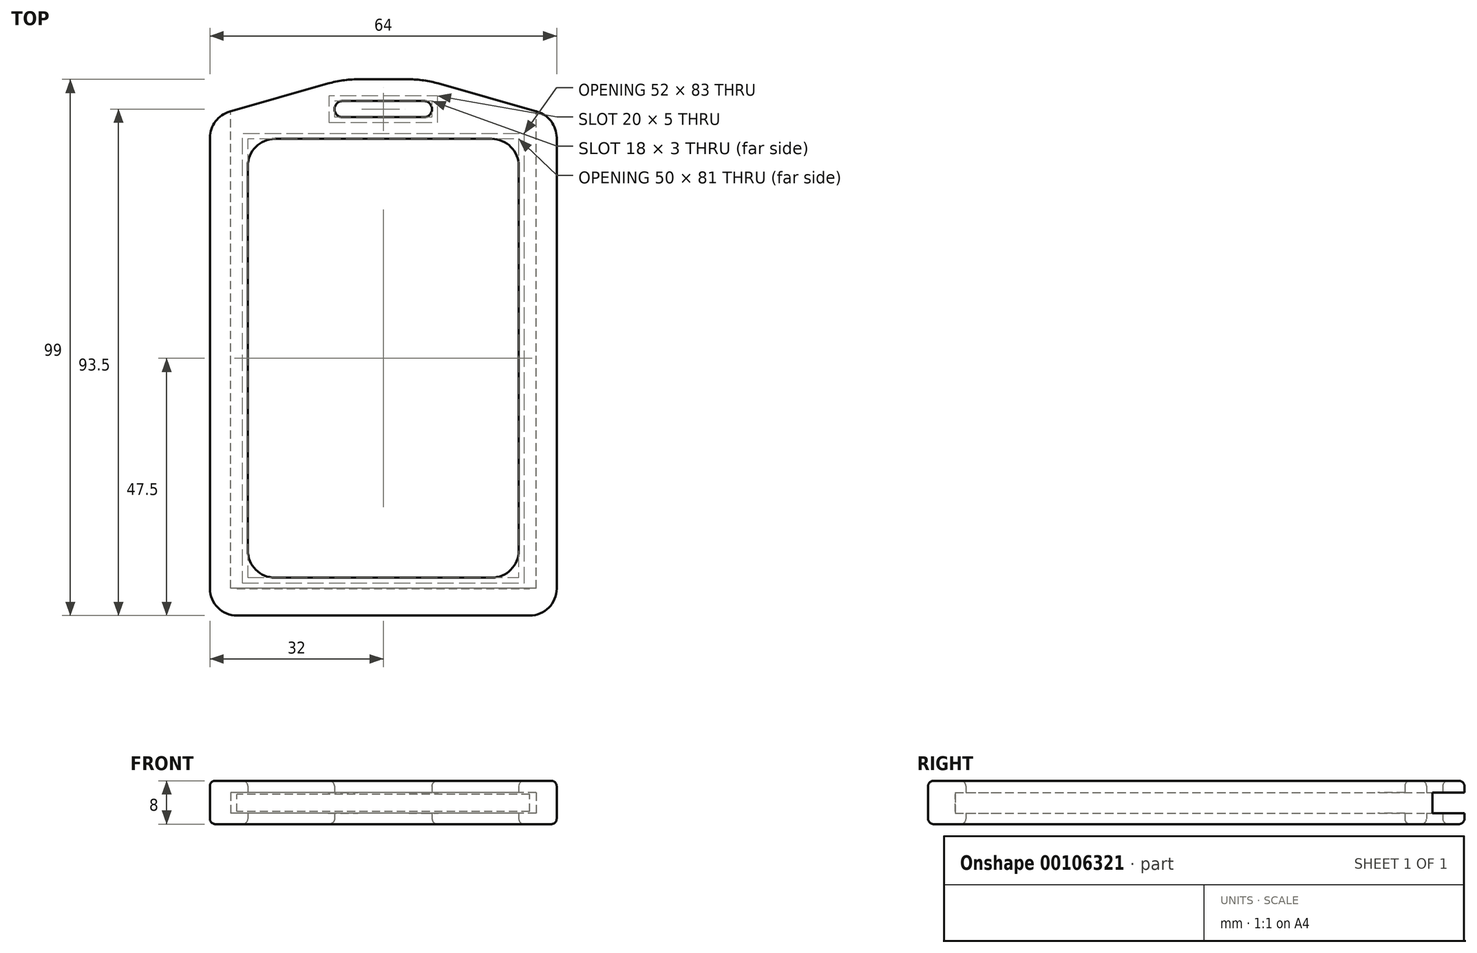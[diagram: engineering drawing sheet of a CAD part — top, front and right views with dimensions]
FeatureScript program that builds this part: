
annotation { "Feature Type Name" : "Feature", "Feature Type Description" : "" }
export const myFeature = defineFeature(function(context is Context, id is Id, definition is map)
    precondition{}
    {
        {
            var Q0;
            Q0=qCreatedBy(makeId("Top.planeOp"),FACE);
            var sketch = newSketch(context, id + "F0", { "sketchPlane" : qUnion([Q0])});
            skLineSegment(sketch, "E0.rect.bottom", {"start": v(-27, 42.5) * mm, "end": v(27, 42.5) * mm});
            skLineSegment(sketch, "E0.rect.top", {"start": v(-27, -42.5) * mm, "end": v(27, -42.5) * mm});
            skLineSegment(sketch, "E0.rect.left", {"start": v(-27, 42.5) * mm, "end": v(-27, -42.5) * mm});
            skLineSegment(sketch, "E0.rect.right", {"start": v(27, 42.5) * mm, "end": v(27, -42.5) * mm});
            skPoint(sketch, "E0.rect.middle", {"position": v(0, 0) * mm});
            skSolve(sketch);
        }
        {
            var Q0;
            Q0=makeQuery(id+"F0.imprint","IMPRINT",FACE,{"disambiguationData":[TD([[makeQuery(id+"F0.imprint","IMPRINT",EDGE,{"derivedFrom":sQuery(id+"F0.wireOp",EDGE,"E0.rect.bottom")}),-1.0]])]});
            extrude(context, id + "F1", {"entities" : qUnion([Q0]), "depth" : 3.2 * mm});
        }
        {
            var Q0;
            Q0=qCreatedBy(makeId("Top.planeOp"),FACE);
            var sketch = newSketch(context, id + "F2", { "sketchPlane" : qUnion([Q0])});
            skLineSegment(sketch, "E1", {"start": v(-32, -47.5) * mm, "end": v(-32, 44.5) * mm});
            skLineSegment(sketch, "E2", {"start": v(32, 44.5) * mm, "end": v(32, -47.5) * mm});
            skLineSegment(sketch, "E3", {"start": v(32, -47.5) * mm, "end": v(-32, -47.5) * mm});
            skLineSegment(sketch, "E4", {"start": v(-7.5, 47.5) * mm, "end": v(7.5, 47.5) * mm});
            skLineSegment(sketch, "E5", {"start": v(-7.5, 44.5) * mm, "end": v(7.5, 44.5) * mm});
            skArc(sketch, "E6", {"start": v(-7.5, 47.5) * mm, "mid": v(-9, 46) * mm, "end": v(-7.5, 44.5) * mm});
            skArc(sketch, "E7", {"start": v(7.5, 47.5) * mm, "mid": v(9, 46) * mm, "end": v(7.5, 44.5) * mm});
            skLineSegment(sketch, "E8.rect.bottom", {"start": v(-25, 40.5) * mm, "end": v(25, 40.5) * mm});
            skLineSegment(sketch, "E8.rect.top", {"start": v(-25, -40.5) * mm, "end": v(25, -40.5) * mm});
            skLineSegment(sketch, "E8.rect.left", {"start": v(-25, 40.5) * mm, "end": v(-25, -40.5) * mm});
            skLineSegment(sketch, "E8.rect.right", {"start": v(25, 40.5) * mm, "end": v(25, -40.5) * mm});
            skPoint(sketch, "E8.rect.middle", {"position": v(0, 0) * mm});
            skLineSegment(sketch, "E9", {"start": v(-32, 44.5) * mm, "end": v(-7.5, 51.5) * mm});
            skLineSegment(sketch, "E10", {"start": v(-7.5, 51.5) * mm, "end": v(7.5, 51.5) * mm});
            skLineSegment(sketch, "E11", {"start": v(7.5, 51.5) * mm, "end": v(32, 44.5) * mm});
            skSolve(sketch);
        }
        {
            var Q0;
            Q0=makeQuery(id+"F2.imprint","IMPRINT",FACE,{"disambiguationData":[TD([[makeQuery(id+"F2.imprint","IMPRINT",EDGE,{"derivedFrom":sQuery(id+"F2.wireOp",EDGE,"E1")}),-1.0]])]});
            var Q1;
            Q1=makeQuery(id+"F2.imprint","IMPRINT",FACE,{"disambiguationData":[TD([[makeQuery(id+"F2.imprint","IMPRINT",EDGE,{"derivedFrom":sQuery(id+"F2.wireOp",EDGE,"E8.rect.bottom")}),1.0]])]});
            extrude(context, id + "F3", {"entities" : qUnion([Q0, Q1]), "depth" : 8 * mm});
        }
        {
            var Q0;
            Q0=makeQuery(id+"F3.opExtrude","SWEPT_EDGE",EDGE,{"disambiguationData":[OSD([sQuery(id+"F2.wireOp",EDGE,"E1"),sQuery(id+"F2.wireOp",EDGE,"bdb59242-d5a5-46b9-b7b7-c48a45b36775")])]});
            var Q1;
            Q1=makeQuery(id+"F3.opExtrude","SWEPT_EDGE",EDGE,{"disambiguationData":[OSD([sQuery(id+"F2.wireOp",EDGE,"daee0165-ca23-428e-b79d-c411e0a02959"),sQuery(id+"F2.wireOp",EDGE,"E2")])]});
            var Q2;
            Q2=makeQuery(id+"F3.opExtrude","SWEPT_EDGE",EDGE,{"disambiguationData":[OSD([sQuery(id+"F2.wireOp",EDGE,"E2"),sQuery(id+"F2.wireOp",EDGE,"E3")])]});
            var Q3;
            Q3=makeQuery(id+"F3.opExtrude","SWEPT_EDGE",EDGE,{"disambiguationData":[OSD([sQuery(id+"F2.wireOp",EDGE,"E1"),sQuery(id+"F2.wireOp",EDGE,"E3")])]});
            fillet(context, id + "F4", {"entities" : qUnion([Q0, Q1, Q2, Q3]), "radius" : 5 * mm, "tangentPropagation" : true, "allowEdgeOverflow" : false});
        }
        {
            var Q0;
            Q0=makeQuery(id+"F3.opExtrude","SWEPT_EDGE",EDGE,{"disambiguationData":[OSD([sQuery(id+"F2.wireOp",EDGE,"E9"),sQuery(id+"F2.wireOp",EDGE,"E10")])]});
            var Q1;
            Q1=makeQuery(id+"F3.opExtrude","SWEPT_EDGE",EDGE,{"disambiguationData":[OSD([sQuery(id+"F2.wireOp",EDGE,"E10"),sQuery(id+"F2.wireOp",EDGE,"E11")])]});
            fillet(context, id + "F5", {"entities" : qUnion([Q0, Q1]), "radius" : 20 * mm, "tangentPropagation" : true, "allowEdgeOverflow" : false});
        }
        {
            var Q0;
            Q0=makeQuery(id+"F3.opExtrude","CAP_EDGE",EDGE,{"disambiguationData":[OSD([sQuery(id+"F2.wireOp",EDGE,"E4")])],"isStart":false});
            var Q1;
            Q1=makeQuery(id+"F3.opExtrude","CAP_EDGE",EDGE,{"disambiguationData":[OSD([sQuery(id+"F2.wireOp",EDGE,"E4")])],"isStart":true});
            fillet(context, id + "F6", {"entities" : qUnion([Q0, Q1]), "radius" : 1 * mm, "tangentPropagation" : true, "allowEdgeOverflow" : false});
        }
        {
            var Q0;
            Q0=makeQuery(id+"F3.opExtrude","SWEPT_EDGE",EDGE,{"disambiguationData":[OSD([sQuery(id+"F2.wireOp",EDGE,"E8.rect.bottom"),sQuery(id+"F2.wireOp",EDGE,"E8.rect.left")])]});
            var Q1;
            Q1=makeQuery(id+"F3.opExtrude","SWEPT_EDGE",EDGE,{"disambiguationData":[OSD([sQuery(id+"F2.wireOp",EDGE,"E8.rect.bottom"),sQuery(id+"F2.wireOp",EDGE,"E8.rect.right")])]});
            var Q2;
            Q2=makeQuery(id+"F3.opExtrude","SWEPT_EDGE",EDGE,{"disambiguationData":[OSD([sQuery(id+"F2.wireOp",EDGE,"E8.rect.top"),sQuery(id+"F2.wireOp",EDGE,"E8.rect.right")])]});
            var Q3;
            Q3=makeQuery(id+"F3.opExtrude","SWEPT_EDGE",EDGE,{"disambiguationData":[OSD([sQuery(id+"F2.wireOp",EDGE,"E8.rect.top"),sQuery(id+"F2.wireOp",EDGE,"E8.rect.left")])]});
            fillet(context, id + "F7", {"entities" : qUnion([Q0, Q1, Q2, Q3]), "radius" : 5 * mm, "tangentPropagation" : true, "allowEdgeOverflow" : false});
        }
        {
            var Q0;
            Q0=makeQuery(id+"F3.opExtrude","CAP_EDGE",EDGE,{"disambiguationData":[OSD([sQuery(id+"F2.wireOp",EDGE,"E8.rect.bottom")])],"isStart":false});
            var Q1;
            Q1=makeQuery(id+"F3.opExtrude","CAP_EDGE",EDGE,{"disambiguationData":[OSD([sQuery(id+"F2.wireOp",EDGE,"E8.rect.bottom")])],"isStart":true});
            var Q2;
            {var subQ0=sQuery(id+"F2.wireOp",EDGE,"E1");var subQ1=sQuery(id+"F2.wireOp",EDGE,"E3");Q2=makeQuery(id+"F4.opFillet","BLEND_EDGE",EDGE,{"blendedFrom":[makeQuery(id+"F3.opExtrude","SWEPT_EDGE",EDGE,{"disambiguationData":[OSD([subQ0,subQ1])]}),makeQuery(id+"F3.opExtrude","CAP_FACE",FACE,{"disambiguationData":[OSD([subQ0,sQuery(id+"F2.wireOp",EDGE,"bdb59242-d5a5-46b9-b7b7-c48a45b36775"),sQuery(id+"F2.wireOp",EDGE,"823fc3bd-2c2f-4f9b-bb1d-b0eb3bebb9c6"),sQuery(id+"F2.wireOp",EDGE,"daee0165-ca23-428e-b79d-c411e0a02959"),sQuery(id+"F2.wireOp",EDGE,"E2"),subQ1,sQuery(id+"F2.wireOp",EDGE,"E4"),sQuery(id+"F2.wireOp",EDGE,"E5"),sQuery(id+"F2.wireOp",EDGE,"E6"),sQuery(id+"F2.wireOp",EDGE,"E7"),sQuery(id+"F2.wireOp",EDGE,"E8.rect.bottom"),sQuery(id+"F2.wireOp",EDGE,"E8.rect.top"),sQuery(id+"F2.wireOp",EDGE,"E8.rect.left"),sQuery(id+"F2.wireOp",EDGE,"E8.rect.right")])],"isStart":false})],"blendedInto":[makeQuery(id+"F3.opExtrude","CAP_FACE",FACE,{"disambiguationData":[OSD([subQ0,sQuery(id+"F2.wireOp",EDGE,"bdb59242-d5a5-46b9-b7b7-c48a45b36775"),sQuery(id+"F2.wireOp",EDGE,"823fc3bd-2c2f-4f9b-bb1d-b0eb3bebb9c6"),sQuery(id+"F2.wireOp",EDGE,"daee0165-ca23-428e-b79d-c411e0a02959"),sQuery(id+"F2.wireOp",EDGE,"E2"),subQ1,sQuery(id+"F2.wireOp",EDGE,"E4"),sQuery(id+"F2.wireOp",EDGE,"E5"),sQuery(id+"F2.wireOp",EDGE,"E6"),sQuery(id+"F2.wireOp",EDGE,"E7"),sQuery(id+"F2.wireOp",EDGE,"E8.rect.bottom"),sQuery(id+"F2.wireOp",EDGE,"E8.rect.top"),sQuery(id+"F2.wireOp",EDGE,"E8.rect.left"),sQuery(id+"F2.wireOp",EDGE,"E8.rect.right")])],"isStart":false})]});}
            var Q3;
            Q3=makeQuery(id+"F3.opExtrude","CAP_EDGE",EDGE,{"disambiguationData":[OSD([sQuery(id+"F2.wireOp",EDGE,"E3")])],"isStart":true});
            fillet(context, id + "F8", {"entities" : qUnion([Q0, Q1, Q2, Q3]), "radius" : 1 * mm, "tangentPropagation" : true, "allowEdgeOverflow" : false});
        }
        {
            var Q0;
            Q0=makeQuery(id+"F1.opExtrude","SWEPT_BODY",BODY,{"disambiguationData":[OSD([sQuery(id+"F0.wireOp",EDGE,"E0.rect.bottom"),sQuery(id+"F0.wireOp",EDGE,"E0.rect.top"),sQuery(id+"F0.wireOp",EDGE,"E0.rect.left"),sQuery(id+"F0.wireOp",EDGE,"E0.rect.right")])]});
            transform(context, id + "F9", {"entities" : qUnion([Q0]), "transformType" : TransformType.TRANSLATION_3D, "dx" : 0 * mm, "dy" : 0 * mm, "dz" : 2.3 * mm, "makeCopy" : false});
        }
        {
            var Q0;
            Q0=makeQuery(id+"F3.opExtrude","SWEPT_FACE",FACE,{"disambiguationData":[OSD([sQuery(id+"F2.wireOp",EDGE,"E10")])]});
            var sketch = newSketch(context, id + "F10", { "sketchPlane" : qUnion([Q0])});
            skLineSegment(sketch, "E12.bottom", {"start": v(-28.2, 5.8) * mm, "end": v(28.2, 5.8) * mm});
            skLineSegment(sketch, "E12.top", {"start": v(-28.2, 2) * mm, "end": v(28.2, 2) * mm});
            skLineSegment(sketch, "E12.left", {"start": v(-28.2, 5.8) * mm, "end": v(-28.2, 2) * mm});
            skLineSegment(sketch, "E12.right", {"start": v(28.2, 5.8) * mm, "end": v(28.2, 2) * mm});
            skSolve(sketch);
        }
        {
            var Q0;
            Q0=qSketchRegion(id+"F10",true);
            extrude(context, id + "F11", {"entities" : qUnion([Q0]), "operationType" : NewBodyOperationType.REMOVE, "oppositeDirection" : true, "depth" : 93.95 * mm});
        }
    });
